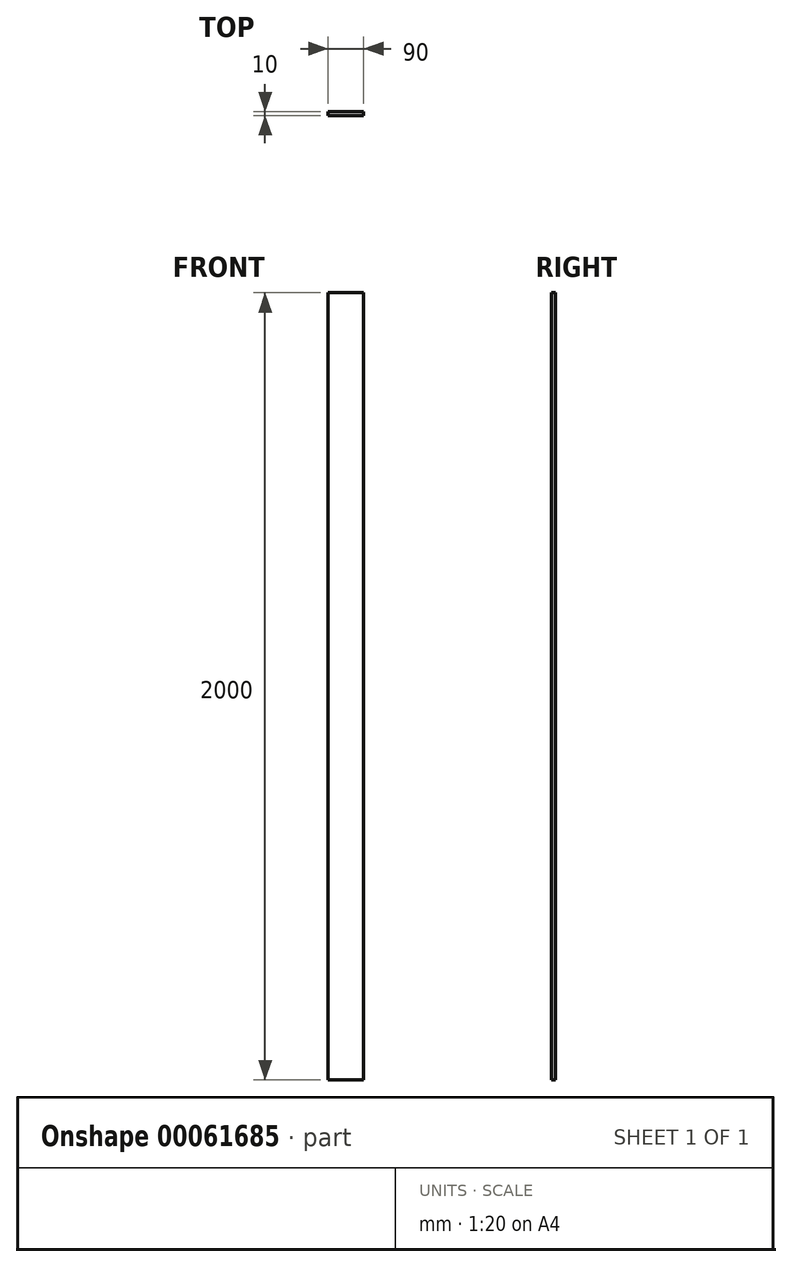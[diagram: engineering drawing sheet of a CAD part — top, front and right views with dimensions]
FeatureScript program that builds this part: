
annotation { "Feature Type Name" : "Feature", "Feature Type Description" : "" }
export const myFeature = defineFeature(function(context is Context, id is Id, definition is map)
    precondition{}
    {
        {
            var Q0;
            Q0=qCreatedBy(makeId("Front.planeOp"),FACE);
            var sketch = newSketch(context, id + "F0", { "sketchPlane" : qUnion([Q0])});
            skLineSegment(sketch, "E0.bottom", {"start": v(0, 0) * mm, "end": v(90, 0) * mm});
            skLineSegment(sketch, "E0.top", {"start": v(0, -2000) * mm, "end": v(90, -2000) * mm});
            skLineSegment(sketch, "E0.left", {"start": v(0, 0) * mm, "end": v(0, -2000) * mm});
            skLineSegment(sketch, "E0.right", {"start": v(90, 0) * mm, "end": v(90, -2000) * mm});
            skSolve(sketch);
        }
        {
            var Q0;
            Q0=makeQuery(id+"F0.imprint","IMPRINT",FACE,{"disambiguationData":[TD([[makeQuery(id+"F0.imprint","IMPRINT",EDGE,{"derivedFrom":sQuery(id+"F0.wireOp",EDGE,"E0.bottom")}),-1.0]])]});
            extrude(context, id + "F1", {"entities" : qUnion([Q0]), "depth" : 10 * mm});
        }
    });
